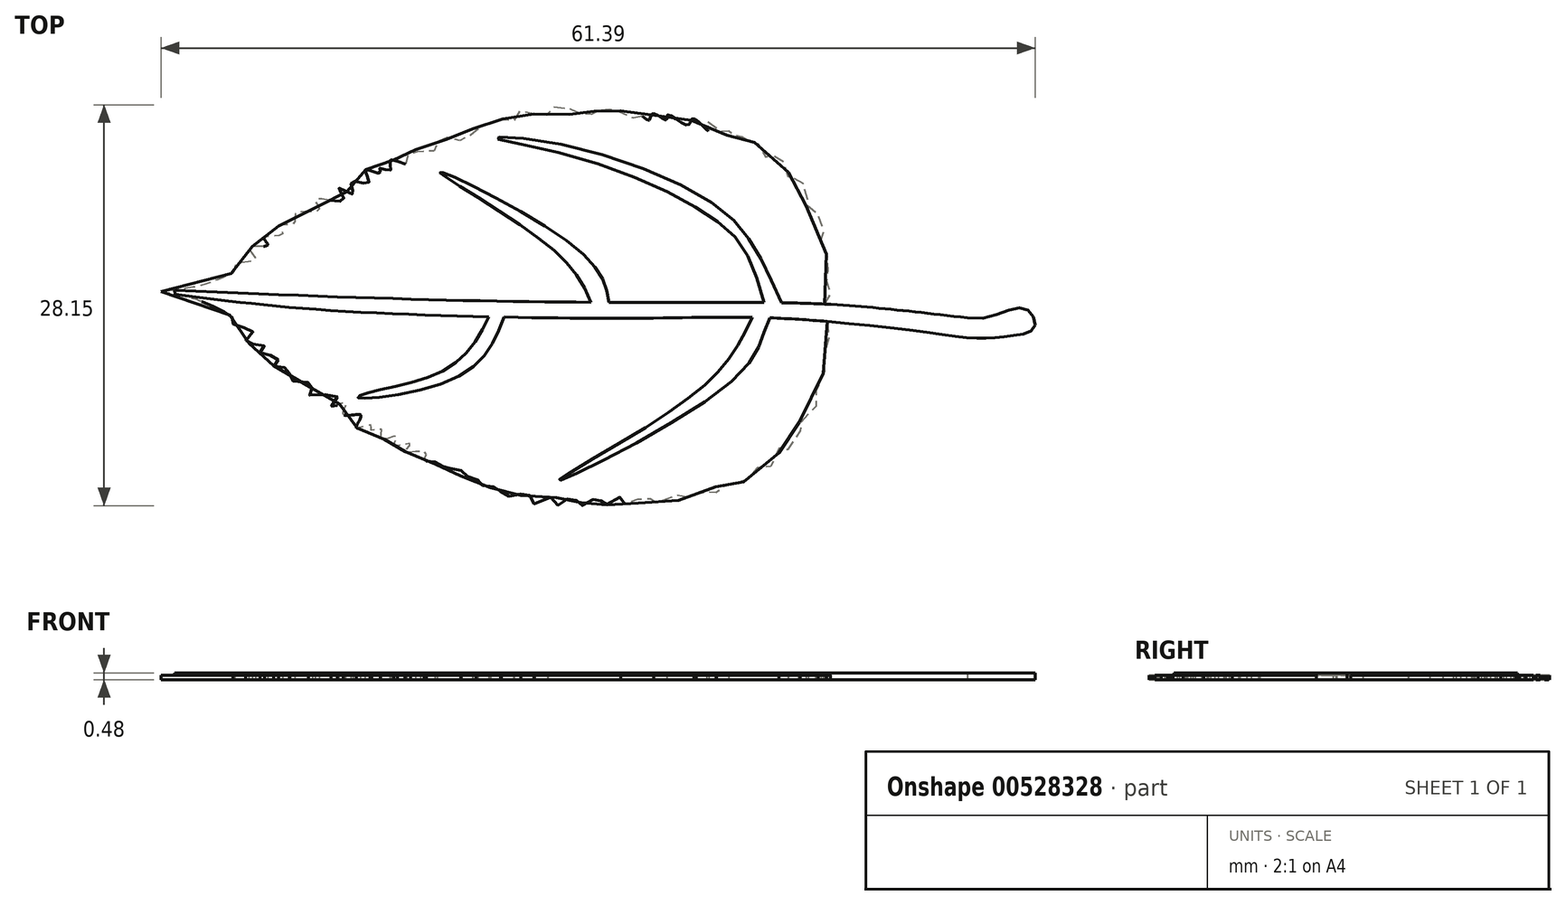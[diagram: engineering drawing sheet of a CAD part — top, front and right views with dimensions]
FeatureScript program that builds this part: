
annotation { "Feature Type Name" : "Feature", "Feature Type Description" : "" }
export const myFeature = defineFeature(function(context is Context, id is Id, definition is map)
    precondition{}
    {
        {
            var Q0;
            Q0=qCreatedBy(makeId("Top.planeOp"),FACE);
            var sketch = newSketch(context, id + "F0", { "sketchPlane" : qUnion([Q0])});
            skFitSpline(sketch, "E0", {"points": [v(-35, 2.42) * mm, v(-33.9, 4.4) * mm, v(-34.71, 7.28) * mm, v(-34.08, 9.35) * mm, v(-35.61, 13.86) * mm, v(-35.07, 15.2) * mm, v(-37.42, 19.53) * mm, v(-38.23, 19.72) * mm, v(-37.87, 21.43) * mm, v(-40.48, 24.85) * mm, v(-41.38, 24.31) * mm, v(-41.47, 26.2) * mm, v(-44.54, 28.73) * mm, v(-45.08, 28) * mm, v(-46.61, 30.53) * mm, v(-47.96, 30.9) * mm, v(-49.31, 31.8) * mm, v(-50.22, 31.52) * mm, v(-51.84, 33.15) * mm, v(-51.93, 32.06) * mm, v(-55.62, 34.5) * mm, v(-55.35, 32.78) * mm, v(-58.06, 35.04) * mm, v(-58.96, 33.87) * mm, v(-62.56, 35.67) * mm, v(-62.74, 34.77) * mm, v(-65.18, 35.85) * mm, v(-65.9, 34.68) * mm, v(-68.24, 36.39) * mm, v(-68.6, 35.04) * mm, v(-70.77, 36.48) * mm, v(-71.13, 35.3) * mm, v(-72.93, 36.66) * mm, v(-73.38, 35.67) * mm, v(-75.1, 36.93) * mm, v(-75.72, 35.67) * mm, v(-77.08, 36.75) * mm, v(-77.98, 35.85) * mm, v(-79.33, 37.2) * mm, v(-79.96, 35.67) * mm, v(-83.48, 37.38) * mm, v(-83.75, 35.58) * mm, v(-85.82, 36.39) * mm, v(-86.09, 35.49) * mm, v(-87.98, 36.12) * mm, v(-89.6, 36.03) * mm, v(-89.6, 34.5) * mm, v(-91.77, 34.95) * mm, v(-92.76, 34.59) * mm, v(-93.93, 34.68) * mm, v(-93.75, 32.87) * mm, v(-96.73, 33.33) * mm, v(-96.82, 32.15) * mm, v(-98.53, 32.24) * mm, v(-99.07, 31.16) * mm, v(-100.51, 32.06) * mm, v(-101.41, 31.25) * mm, v(-101.68, 30.53) * mm, v(-103.4, 30.98) * mm, v(-103.12, 29.45) * mm, v(-106.82, 29.63) * mm, v(-105.92, 28.19) * mm, v(-108.8, 28.64) * mm, v(-108.35, 27.02) * mm, v(-111.24, 27.74) * mm, v(-111.24, 25.93) * mm, v(-113.13, 26.3) * mm, v(-113.04, 25.4) * mm, v(-115.65, 26.02) * mm, v(-115.02, 23.77) * mm, v(-118.09, 23.86) * mm, v(-117.82, 21.79) * mm, v(-120.34, 22.78) * mm, v(-119.44, 20.7) * mm, v(-124.4, 20.8) * mm, v(-123.77, 19) * mm, v(-127.82, 18.36) * mm, v(-128.18, 16.56) * mm, v(-130.89, 16.2) * mm, v(-130.16, 14.76) * mm, v(-133.4, 14.04) * mm, v(-132.78, 12.77) * mm, v(-136.11, 12.32) * mm, v(-134.94, 10.34) * mm, v(-138.37, 9.44) * mm, v(-138.64, 8.36) * mm, v(-140.62, 7.1) * mm, v(-144.68, 5.65) * mm, v(-151.62, 4.57) * mm], "startDerivative": vector(154.24, 139.17) * mm, "endDerivative": vector(-359.14, -41.4) * mm});
            skFitSpline(sketch, "E1.MirrorCS", {"points": [v(-34.51, -0.63) * mm, v(-34.17, -3.36) * mm, v(-35.18, -6.18) * mm, v(-34.7, -8.3) * mm, v(-36.53, -12.68) * mm, v(-36.08, -14.07) * mm, v(-38.72, -18.22) * mm, v(-39.54, -18.35) * mm, v(-39.3, -20.08) * mm, v(-42.14, -23.31) * mm, v(-43, -22.72) * mm, v(-43.23, -24.6) * mm, v(-46.46, -26.9) * mm, v(-46.95, -26.15) * mm, v(-48.65, -28.56) * mm, v(-50.02, -28.83) * mm, v(-51.43, -29.63) * mm, v(-52.31, -29.3) * mm, v(-54.04, -30.8) * mm, v(-54.06, -29.72) * mm, v(-57.91, -31.9) * mm, v(-57.53, -30.2) * mm, v(-60.38, -32.26) * mm, v(-61.2, -31.04) * mm, v(-64.92, -32.58) * mm, v(-65.04, -31.67) * mm, v(-67.54, -32.58) * mm, v(-68.18, -31.37) * mm, v(-70.63, -32.91) * mm, v(-70.9, -31.54) * mm, v(-73.16, -32.83) * mm, v(-73.44, -31.64) * mm, v(-75.33, -32.86) * mm, v(-75.7, -31.84) * mm, v(-77.5, -32.98) * mm, v(-78.05, -31.68) * mm, v(-79.47, -32.66) * mm, v(-80.3, -31.7) * mm, v(-81.75, -32.96) * mm, v(-82.27, -31.39) * mm, v(-85.9, -32.85) * mm, v(-86.04, -31.04) * mm, v(-88.17, -31.7) * mm, v(-88.38, -30.79) * mm, v(-90.3, -31.28) * mm, v(-91.92, -31.08) * mm, v(-91.81, -29.55) * mm, v(-94, -29.85) * mm, v(-94.97, -29.43) * mm, v(-96.14, -29.43) * mm, v(-95.84, -27.65) * mm, v(-98.84, -27.9) * mm, v(-98.85, -26.72) * mm, v(-100.56, -26.69) * mm, v(-101.03, -25.57) * mm, v(-102.53, -26.37) * mm, v(-103.37, -25.5) * mm, v(-103.59, -24.77) * mm, v(-105.33, -25.1) * mm, v(-104.95, -23.59) * mm, v(-108.65, -23.51) * mm, v(-107.66, -22.14) * mm, v(-110.56, -22.38) * mm, v(-110, -20.8) * mm, v(-112.93, -21.32) * mm, v(-112.8, -19.52) * mm, v(-114.72, -19.75) * mm, v(-114.57, -18.86) * mm, v(-117.22, -19.3) * mm, v(-116.43, -17.1) * mm, v(-119.5, -16.98) * mm, v(-119.08, -14.93) * mm, v(-121.67, -15.74) * mm, v(-120.63, -13.74) * mm, v(-125.58, -13.49) * mm, v(-124.83, -11.73) * mm, v(-128.83, -10.82) * mm, v(-129.06, -9) * mm, v(-131.73, -8.45) * mm, v(-130.92, -7.07) * mm, v(-134.1, -6.12) * mm, v(-133.39, -4.9) * mm, v(-136.68, -4.23) * mm, v(-135.38, -2.33) * mm, v(-138.73, -1.2) * mm, v(-138.93, -0.14) * mm, v(-140.82, 1.3) * mm, v(-144.75, 3.01) * mm, v(-151.53, 4.59) * mm], "startDerivative": vector(144.29, -149.47) * mm, "endDerivative": vector(-355.45, 66) * mm});
            skFitSpline(sketch, "E2", {"points": [v(-9.89, 0) * mm, v(-35, 2.42) * mm, v(-72.87, 2.73) * mm, v(-149.14, 4.86) * mm], "startDerivative": vector(-113.83, 12.88) * mm, "endDerivative": vector(-209.8, 9.63) * mm});
            skFitSpline(sketch, "E3", {"points": [v(-149.1, 4.14) * mm, v(-124.77, 1.53) * mm, v(-83.39, 0) * mm, v(-61.83, 0) * mm, v(-41.45, -0.14) * mm, v(-16.28, -2.66) * mm, v(-7.38, -3.6) * mm, v(-2.28, -3.16) * mm, v(1.88, -1.58) * mm, v(0, 1.7) * mm, v(-9.89, 0) * mm], "startDerivative": vector(166.9, -20.3) * mm, "endDerivative": vector(-149.4, 29.37) * mm});
            skFitSpline(sketch, "E4", {"points": [v(-42.57, 2.66) * mm, v(-47.07, 11.99) * mm, v(-54.64, 20.1) * mm, v(-81.41, 30.54) * mm, v(-92.78, 31.6) * mm, v(-78.23, 28.11) * mm, v(-57.16, 19.17) * mm, v(-49.43, 12.5) * mm, v(-45.64, 2.7) * mm], "startDerivative": vector(-39.93, 92.66) * mm, "endDerivative": vector(27.98, -100.65) * mm});
            skFitSpline(sketch, "E5", {"points": [v(-44.58, 0) * mm, v(-50.6, -10.5) * mm, v(-81.7, -28.62) * mm, v(-66.37, -19.18) * mm, v(-52.43, -8.04) * mm, v(-47.72, 0.08) * mm], "startDerivative": vector(-29.96, -57.52) * mm, "endDerivative": vector(27.24, 56.36) * mm});
            skFitSpline(sketch, "E6", {"points": [v(-72.87, 2.73) * mm, v(-79.02, 12.6) * mm, v(-102.52, 25.64) * mm, v(-86.6, 15.02) * mm, v(-76.01, 2.74) * mm], "startDerivative": vector(-5.41, 47.45) * mm, "endDerivative": vector(22.98, -61.13) * mm});
            skFitSpline(sketch, "E7", {"points": [v(-91.3, 0.14) * mm, v(-99.6, -10.46) * mm, v(-116.93, -14.02) * mm, v(-115.53, -13.26) * mm, v(-101.76, -9.18) * mm, v(-94, 0.2) * mm], "startDerivative": vector(-20.68, -54.85) * mm, "endDerivative": vector(23.42, 52.78) * mm});
            skLineSegment(sketch, "E8", {"start": v(-149.14, 4.86) * mm, "end": v(-149.1, 4.14) * mm});
            skLineSegment(sketch, "E9", {"start": v(-151.53, 4.59) * mm, "end": v(-151.62, 4.57) * mm});
            skSolve(sketch);
        }
        {
            var Q0;
            {var subQ11=sQuery(id+"F0.wireOp",EDGE,"E4");Q0=makeQuery(id+"F0.imprint","IMPRINT",FACE,{"disambiguationData":[TD([[makeQuery(id+"F0.imprint","IMPRINT",EDGE,{"derivedFrom":subQ11}),-1.0]])]});}
            extrude(context, id + "F1", {"entities" : qUnion([Q0]), "depth" : 0.8 * mm});
        }
        {
            var Q0;
            {var subQ4=sQuery(id+"F0.wireOp",EDGE,"E8");Q0=makeQuery(id+"F0.imprint","IMPRINT",FACE,{"disambiguationData":[TD([[makeQuery(id+"F0.imprint","IMPRINT",EDGE,{"derivedFrom":subQ4}),1.0]])]});}
            var Q1;
            {var subQ0=sQuery(id+"F0.wireOp",EDGE,"E6");Q1=makeQuery(id+"F0.imprint","IMPRINT",FACE,{"disambiguationData":[TD([[makeQuery(id+"F0.imprint","IMPRINT",EDGE,{"derivedFrom":subQ0}),1.0]])]});}
            var Q2;
            {var subQ0=sQuery(id+"F0.wireOp",EDGE,"E4");Q2=makeQuery(id+"F0.imprint","IMPRINT",FACE,{"disambiguationData":[TD([[makeQuery(id+"F0.imprint","IMPRINT",EDGE,{"derivedFrom":subQ0}),1.0]])]});}
            var Q3;
            {var subQ0=sQuery(id+"F0.wireOp",EDGE,"E5");Q3=makeQuery(id+"F0.imprint","IMPRINT",FACE,{"disambiguationData":[TD([[makeQuery(id+"F0.imprint","IMPRINT",EDGE,{"derivedFrom":subQ0}),-1.0]])]});}
            var Q4;
            {var subQ0=sQuery(id+"F0.wireOp",EDGE,"E7");Q4=makeQuery(id+"F0.imprint","IMPRINT",FACE,{"disambiguationData":[TD([[makeQuery(id+"F0.imprint","IMPRINT",EDGE,{"derivedFrom":subQ0}),-1.0]])]});}
            extrude(context, id + "F2", {"entities" : qUnion([Q0, Q1, Q2, Q3, Q4]), "operationType" : NewBodyOperationType.ADD, "depth" : 1.2 * mm});
        }
        {
            var Q0;
            Q0=makeQuery(id+"F1.opExtrude","SWEPT_BODY",BODY,{"disambiguationData":[OSD([sQuery(id+"F0.wireOp",EDGE,"E0"),sQuery(id+"F0.wireOp",EDGE,"E1.MirrorCS"),sQuery(id+"F0.wireOp",EDGE,"E2"),sQuery(id+"F0.wireOp",EDGE,"E3"),sQuery(id+"F0.wireOp",EDGE,"E4"),sQuery(id+"F0.wireOp",EDGE,"E5"),sQuery(id+"F0.wireOp",EDGE,"E6"),sQuery(id+"F0.wireOp",EDGE,"E7"),sQuery(id+"F0.wireOp",EDGE,"E8")])]});
            var Q1;
            Q1=qCreatedBy(makeId("Origin.pointOp"),VERTEX);
            transform(context, id + "F3", {"entities" : qUnion([Q0]), "transformType" : TransformType.SCALE_UNIFORMLY, "scale" : 0.4, "scalePoint" : qUnion([Q1]), "makeCopy" : false});
        }
    });
